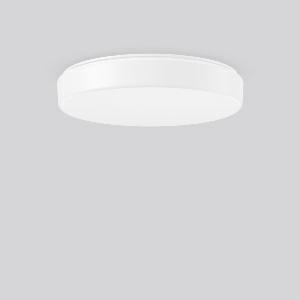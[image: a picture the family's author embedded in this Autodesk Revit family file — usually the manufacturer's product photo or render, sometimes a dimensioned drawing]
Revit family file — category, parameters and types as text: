
# Revit family: flat_polymero_kreis_672392_002_1_ad0b
name_source: partatom
category: Lighting Fixtures
units: mm (PartAtom-declared; Revit-internal decimal feet)

## family parameters
Cut with Voids When Loaded = No
Host = Face
Light Source = No
Part Type = Normal
Room Calculation Point = No
Round Connector Dimension = Use Diameter
Shared = No

## types (1)
- FLAT POLYMERO KREIS (1 x LED Modul 840, 2600 lm, 4000)
    Apparent Load = 23 VA
    CIE Flux Codes = 42 72 91 84 100
    Color Rendering = 80
    Color Temperature = 4000
    Default Elevation = 1800 mm
    Description = Series: FLAT POLYMERO KREIS
Decorative round surface-mounted luminaire. For escape route illumination. Base: metal, powder-coated. Diffuser made of non-yellowing plastic (PMMA), opal. Diffuser fastening: patented push system. Suitable for Ceiling mounting, Wall (surface). Driver integrated. Suitable for connection to central battery systems. 
Colour: white
Diameter: 515 mm
Height: 98 mm
Weight: 2.8 kg
Operating mode: Combined NL readiness
Lamp: LED
Socket: without socket
Colour temperature: 4000K
Colour rendering index (CRI): 80
System power: 23 W
Rated luminous flux: 2600 lm
Luminous flux, emergency: 550 lm
System power, emergency: 5.9 W
Control gear: Regulated power supply
Protection class: I
Type of protection: IP 40
    Height = 98 mm
    Lamp = 1 x LED Modul 840
    Lamp Light Flux = 2600 lm
    Lamp count = 1
    Length = 515 mm
    Lifetime = 50000 h
    Luminous efficacy = 113 lm/W
    Manufacturer = RZB
    ModVariant = No
    Model = 672392.002.1
    Mounting Place = Ceiling, Wall
    Mounting Type = Surface mounted
    Number of Poles = 1
    OnlyDefault = Yes
    Power Factor = 1
    Product Name = FLAT POLYMERO KREIS
    Product group = Surface mounted ceiling and wall luminaires
    ProductGroupID = 305
    Protection Class = Protection class I
    Protection Degree = IP 40
    RLX_Detail_Level = 1
    RLX_Emergency_Light_Flux = 550 lm
    RLX_Emergency_Type = 3
    RLX_Emergency_Type_DB = Yes
    RlxData = <blob elided: 56909 chars, md5=2a98d4e0>
    Socket = socket
    Standby Power = 0 W
    System Light Flux = 2600 lm
    System Power = 23 W
    Type Comments = Product without accessories
    Type Image = 311604.862.79.jpg
    URL = http://relux.com
    VarID = ---
    Voltage = 230 V
    Voltage Range = 220-240 V
    Weight = 0.00 kg
    Width = 0 mm  [stored 0 ft]

note: [stored X ft] marks values corroborated as IEEE doubles in the binary element streams (Revit-internal decimal feet)

## geometry (parser evidence)
native form markers: Blend x4, Sweep x13
no freeform markers — native parametric forms only
